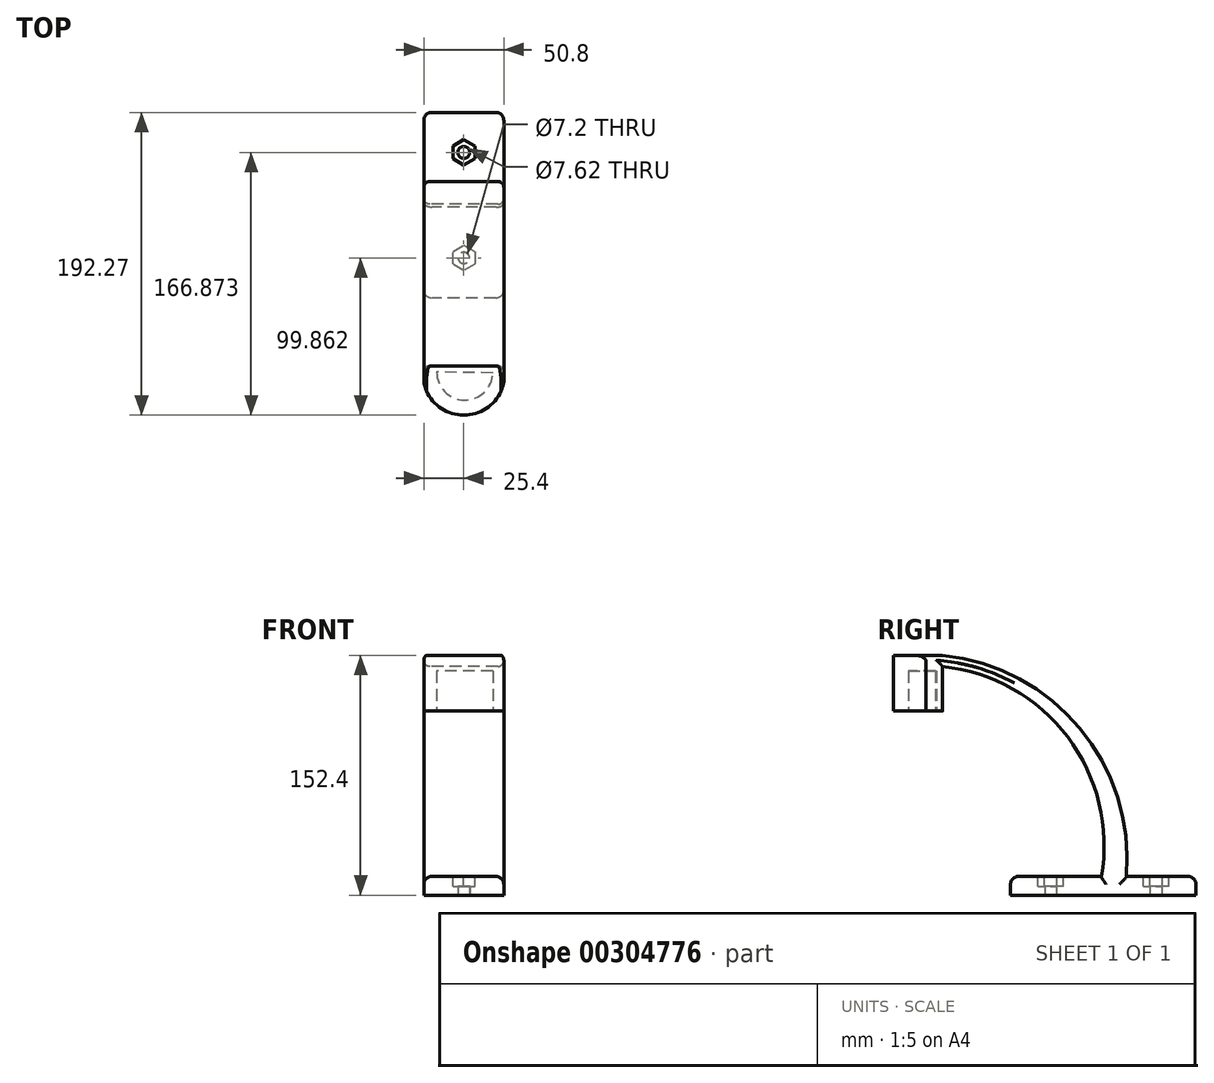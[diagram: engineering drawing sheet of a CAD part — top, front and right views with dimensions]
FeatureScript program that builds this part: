
annotation { "Feature Type Name" : "Feature", "Feature Type Description" : "" }
export const myFeature = defineFeature(function(context is Context, id is Id, definition is map)
    precondition{}
    {
        {
            var Q0;
            Q0=qCreatedBy(makeId("Right.planeOp"),FACE);
            var sketch = newSketch(context, id + "F0", { "sketchPlane" : qUnion([Q0])});
            skLineSegment(sketch, "E0.bottom", {"start": v(-57.77, 0) * mm, "end": v(60.04, 0) * mm});
            skLineSegment(sketch, "E0.top", {"start": v(-57.77, 11.91) * mm, "end": v(60.04, 11.91) * mm});
            skLineSegment(sketch, "E0.left", {"start": v(-57.77, 0) * mm, "end": v(-57.77, 11.91) * mm});
            skLineSegment(sketch, "E0.right", {"start": v(60.04, 0) * mm, "end": v(60.04, 11.91) * mm});
            skLineSegment(sketch, "E1.bottom", {"start": v(-132.44, 117) * mm, "end": v(-100.9, 117) * mm});
            skLineSegment(sketch, "E1.top", {"start": v(-132.44, 152.4) * mm, "end": v(-100.9, 152.4) * mm});
            skLineSegment(sketch, "E1.left", {"start": v(-132.44, 117) * mm, "end": v(-132.44, 152.4) * mm});
            skLineSegment(sketch, "E1.right", {"start": v(-100.9, 117) * mm, "end": v(-100.9, 152.4) * mm});
            skArc(sketch, "E2", {"start": v(15.8, 11.91) * mm, "mid": v(-13.86, 106) * mm, "end": v(-100.9, 152.4) * mm});
            skArc(sketch, "E3", {"start": v(0, 11.91) * mm, "mid": v(-21.52, 100.47) * mm, "end": v(-100.9, 145.2) * mm});
            skSolve(sketch);
        }
        {
            var Q0;
            Q0=qSketchRegion(id+"F0",true);
            extrude(context, id + "F1", {"entities" : qUnion([Q0]), "depth" : 50.8 * mm});
        }
        {
            var Q0;
            Q0=makeQuery(id+"F1.opExtrude","SWEPT_FACE",FACE,{"disambiguationData":[OSD([sQuery(id+"F0.wireOp",EDGE,"E1.top")])]});
            var sketch = newSketch(context, id + "F2", { "sketchPlane" : qUnion([Q0])});
            skArc(sketch, "E4", {"start": v(0, -100.9) * mm, "mid": v(25.4, -132.23) * mm, "end": v(50.8, -100.9) * mm});
            skSolve(sketch);
        }
        {
            var Q0;
            {var subQ0=sQuery(id+"F0.wireOp",EDGE,"E1.top");var subQ4=makeQuery(id+"F1.opExtrude","SWEPT_EDGE",EDGE,{"disambiguationData":[OSD([subQ0,sQuery(id+"F0.wireOp",EDGE,"E1.left")])]});Q0=makeQuery(id+"F2.imprint","IMPRINT",FACE,{"disambiguationData":[TD([[makeQuery(id+"F2.imprint","IMPRINT",EDGE,{"derivedFrom":subQ4}),-1.0]])]});}
            extrude(context, id + "F3", {"entities" : qUnion([Q0]), "operationType" : NewBodyOperationType.REMOVE, "endBound" : BoundingType.UP_TO_NEXT, "oppositeDirection" : true, "depth" : 25.4 * mm});
        }
        {
            var Q0;
            Q0=makeQuery(id+"F1.opExtrude","CAP_EDGE",EDGE,{"disambiguationData":[OSD([sQuery(id+"F0.wireOp",EDGE,"E1.right")])],"isStart":false});
            var Q1;
            Q1=makeQuery(id+"F1.opExtrude","CAP_EDGE",EDGE,{"disambiguationData":[OSD([sQuery(id+"F0.wireOp",EDGE,"E1.right")])],"isStart":true});
            var Q2;
            Q2=makeQuery(id+"F1.opExtrude","CAP_EDGE",EDGE,{"disambiguationData":[OSD([sQuery(id+"F0.wireOp",EDGE,"E3")])],"isStart":false});
            var Q3;
            Q3=makeQuery(id+"F1.opExtrude","CAP_EDGE",EDGE,{"disambiguationData":[OSD([sQuery(id+"F0.wireOp",EDGE,"E2")])],"isStart":false});
            var Q4;
            Q4=makeQuery(id+"F3.boolean.opBoolean","COPY",EDGE,{"derivedFrom":makeQuery(id+"F3.opExtrude","CAP_EDGE",EDGE,{"disambiguationData":[OSD([sQuery(id+"F2.wireOp",EDGE,"E4")])],"isStart":false})});
            var Q5;
            Q5=makeQuery(id+"F1.opExtrude","CAP_EDGE",EDGE,{"disambiguationData":[OSD([sQuery(id+"F0.wireOp",EDGE,"E3")])],"isStart":true});
            var Q6;
            Q6=makeQuery(id+"F1.opExtrude","CAP_EDGE",EDGE,{"disambiguationData":[OSD([sQuery(id+"F0.wireOp",EDGE,"E2")])],"isStart":true});
            fillet(context, id + "F4", {"entities" : qUnion([Q0, Q1, Q2, Q3, Q4, Q5, Q6]), "radius" : 3.8 * mm, "tangentPropagation" : true, "allowEdgeOverflow" : false});
        }
        {
            var Q0;
            Q0=makeQuery(id+"F1.opExtrude","SWEPT_FACE",FACE,{"disambiguationData":[OSD([sQuery(id+"F0.wireOp",EDGE,"E1.bottom")])]});
            var sketch = newSketch(context, id + "F5", { "sketchPlane" : qUnion([Q0])});
            skArc(sketch, "E5", {"start": v(43.42, 100.9) * mm, "mid": v(26.02, 122.66) * mm, "end": v(8.61, 100.9) * mm});
            skLineSegment(sketch, "E6", {"start": v(43.84, 105.46) * mm, "end": v(8.18, 104.82) * mm});
            skSolve(sketch);
        }
        {
            var Q0;
            {var subQ0=sQuery(id+"F5.wireOp",EDGE,"E6");Q0=makeQuery(id+"F5.imprint","IMPRINT",FACE,{"disambiguationData":[TD([[makeQuery(id+"F5.imprint","IMPRINT",EDGE,{"derivedFrom":subQ0}),-1.0]])]});}
            extrude(context, id + "F6", {"entities" : qUnion([Q0]), "operationType" : NewBodyOperationType.REMOVE, "oppositeDirection" : true, "depth" : 25.4 * mm});
        }
        {
            var Q0;
            {var subQ0=sQuery(id+"F0.wireOp",EDGE,"E0.top");Q0=makeQuery(id+"F1.opExtrude","SWEPT_FACE",FACE,{"disambiguationData":[OSD([subQ0]),TDD([makeQuery(id+"F0.imprint","IMPRINT",EDGE,{"disambiguationData":[TD([[makeQuery(id+"F0.imprint","INTERSECT",VERTEX,{"derivedFrom":[subQ0,sQuery(id+"F0.wireOp",EDGE,"E0.left")]}),-1.0]])],"derivedFrom":subQ0})])]});}
            var sketch = newSketch(context, id + "F7", { "sketchPlane" : qUnion([Q0])});
            skCircle(sketch, "E7.cCircle", {"center": v(25.4, -32.37) * mm, "radius": 6.99 * mm, "construction": true});
            skLineSegment(sketch, "E7.0", {"start": v(32.39, -28.33) * mm, "end": v(32.39, -36.4) * mm});
            skLineSegment(sketch, "E7.1", {"start": v(32.39, -36.4) * mm, "end": v(25.4, -40.43) * mm});
            skLineSegment(sketch, "E7.2", {"start": v(25.4, -40.43) * mm, "end": v(18.41, -36.4) * mm});
            skLineSegment(sketch, "E7.3", {"start": v(18.41, -36.4) * mm, "end": v(18.41, -28.33) * mm});
            skLineSegment(sketch, "E7.4", {"start": v(18.41, -28.33) * mm, "end": v(25.4, -24.3) * mm});
            skLineSegment(sketch, "E7.5", {"start": v(25.4, -24.3) * mm, "end": v(32.39, -28.33) * mm});
            skPoint(sketch, "E7.0.midPoint", {"position": v(32.39, -32.37) * mm});
            skSolve(sketch);
        }
        {
            var Q0;
            {var subQ0=sQuery(id+"F0.wireOp",EDGE,"E0.top");Q0=makeQuery(id+"F1.opExtrude","SWEPT_FACE",FACE,{"disambiguationData":[OSD([subQ0]),TDD([makeQuery(id+"F0.imprint","IMPRINT",EDGE,{"disambiguationData":[TD([[makeQuery(id+"F0.imprint","INTERSECT",VERTEX,{"derivedFrom":[subQ0,sQuery(id+"F0.wireOp",EDGE,"E0.right")]}),1.0]])],"derivedFrom":subQ0})])]});}
            var sketch = newSketch(context, id + "F8", { "sketchPlane" : qUnion([Q0])});
            skCircle(sketch, "E8.cCircle", {"center": v(25.4, 34.64) * mm, "radius": 6.98 * mm, "construction": true});
            skLineSegment(sketch, "E8.0", {"start": v(32.38, 38.68) * mm, "end": v(32.38, 30.6) * mm});
            skLineSegment(sketch, "E8.1", {"start": v(32.39, 30.6) * mm, "end": v(25.4, 26.58) * mm});
            skLineSegment(sketch, "E8.2", {"start": v(25.4, 26.58) * mm, "end": v(18.41, 30.6) * mm});
            skLineSegment(sketch, "E8.3", {"start": v(18.41, 30.6) * mm, "end": v(18.41, 38.68) * mm});
            skLineSegment(sketch, "E8.4", {"start": v(18.41, 38.68) * mm, "end": v(25.4, 42.7) * mm});
            skLineSegment(sketch, "E8.5", {"start": v(25.4, 42.7) * mm, "end": v(32.38, 38.68) * mm});
            skPoint(sketch, "E8.0.midPoint", {"position": v(32.38, 34.64) * mm});
            skSolve(sketch);
        }
        {
            var Q0;
            Q0=makeQuery(id+"F7.imprint","IMPRINT",FACE,{"disambiguationData":[TD([[makeQuery(id+"F7.imprint","IMPRINT",EDGE,{"derivedFrom":sQuery(id+"F7.wireOp",EDGE,"E7.0")}),-1.0]])]});
            var Q1;
            Q1=makeQuery(id+"F8.imprint","IMPRINT",FACE,{"disambiguationData":[TD([[makeQuery(id+"F8.imprint","IMPRINT",EDGE,{"derivedFrom":sQuery(id+"F8.wireOp",EDGE,"E8.0")}),-1.0]])]});
            extrude(context, id + "F9", {"entities" : qUnion([Q0, Q1]), "operationType" : NewBodyOperationType.REMOVE, "oppositeDirection" : true, "depth" : 6.35 * mm});
        }
        {
            var Q0;
            Q0=makeQuery(id+"F1.opExtrude","CAP_EDGE",EDGE,{"disambiguationData":[OSD([sQuery(id+"F0.wireOp",EDGE,"E0.right")])],"isStart":false});
            var Q1;
            Q1=makeQuery(id+"F1.opExtrude","CAP_EDGE",EDGE,{"disambiguationData":[OSD([sQuery(id+"F0.wireOp",EDGE,"E0.left")])],"isStart":false});
            var Q2;
            Q2=makeQuery(id+"F1.opExtrude","CAP_EDGE",EDGE,{"disambiguationData":[OSD([sQuery(id+"F0.wireOp",EDGE,"E0.right")])],"isStart":true});
            var Q3;
            Q3=makeQuery(id+"F1.opExtrude","CAP_EDGE",EDGE,{"disambiguationData":[OSD([sQuery(id+"F0.wireOp",EDGE,"E0.left")])],"isStart":true});
            var Q4;
            {var subQ0=sQuery(id+"F0.wireOp",EDGE,"E0.top");Q4=makeQuery(id+"F1.opExtrude","CAP_EDGE",EDGE,{"disambiguationData":[OSD([subQ0]),TDD([makeQuery(id+"F0.imprint","IMPRINT",EDGE,{"disambiguationData":[TD([[makeQuery(id+"F0.imprint","INTERSECT",VERTEX,{"derivedFrom":[subQ0,sQuery(id+"F0.wireOp",EDGE,"E0.right")]}),1.0]])],"derivedFrom":subQ0})])],"isStart":true});}
            var Q5;
            {var subQ0=sQuery(id+"F0.wireOp",EDGE,"E0.top");Q5=makeQuery(id+"F1.opExtrude","CAP_EDGE",EDGE,{"disambiguationData":[OSD([subQ0]),TDD([makeQuery(id+"F0.imprint","IMPRINT",EDGE,{"disambiguationData":[TD([[makeQuery(id+"F0.imprint","INTERSECT",VERTEX,{"derivedFrom":[subQ0,sQuery(id+"F0.wireOp",EDGE,"E0.left")]}),-1.0]])],"derivedFrom":subQ0})])],"isStart":true});}
            var Q6;
            {var subQ0=sQuery(id+"F0.wireOp",EDGE,"E0.top");Q6=makeQuery(id+"F1.opExtrude","CAP_EDGE",EDGE,{"disambiguationData":[OSD([subQ0]),TDD([makeQuery(id+"F0.imprint","IMPRINT",EDGE,{"disambiguationData":[TD([[makeQuery(id+"F0.imprint","INTERSECT",VERTEX,{"derivedFrom":[subQ0,sQuery(id+"F0.wireOp",EDGE,"E0.right")]}),1.0]])],"derivedFrom":subQ0})])],"isStart":false});}
            var Q7;
            {var subQ0=sQuery(id+"F0.wireOp",EDGE,"E0.top");Q7=makeQuery(id+"F1.opExtrude","CAP_EDGE",EDGE,{"disambiguationData":[OSD([subQ0]),TDD([makeQuery(id+"F0.imprint","IMPRINT",EDGE,{"disambiguationData":[TD([[makeQuery(id+"F0.imprint","INTERSECT",VERTEX,{"derivedFrom":[subQ0,sQuery(id+"F0.wireOp",EDGE,"E0.left")]}),-1.0]])],"derivedFrom":subQ0})])],"isStart":false});}
            var Q8;
            Q8=makeQuery(id+"F1.opExtrude","SWEPT_EDGE",EDGE,{"disambiguationData":[OSD([sQuery(id+"F0.wireOp",EDGE,"E0.top"),sQuery(id+"F0.wireOp",EDGE,"E0.left")])]});
            var Q9;
            Q9=makeQuery(id+"F1.opExtrude","SWEPT_EDGE",EDGE,{"disambiguationData":[OSD([sQuery(id+"F0.wireOp",EDGE,"E0.top"),sQuery(id+"F0.wireOp",EDGE,"E0.right")])]});
            fillet(context, id + "F10", {"entities" : qUnion([Q0, Q1, Q2, Q3, Q4, Q5, Q6, Q7, Q8, Q9]), "radius" : 5.08 * mm, "tangentPropagation" : true, "allowEdgeOverflow" : false});
        }
        {
            var Q0;
            Q0=makeQuery(id+"F1.opExtrude","SWEPT_FACE",FACE,{"disambiguationData":[OSD([sQuery(id+"F0.wireOp",EDGE,"E0.bottom")])]});
            var sketch = newSketch(context, id + "F11", { "sketchPlane" : qUnion([Q0])});
            skCircle(sketch, "E9", {"center": v(25.4, 32.37) * mm, "radius": 3.6 * mm});
            skCircle(sketch, "E10", {"center": v(25.4, -34.64) * mm, "radius": 3.81 * mm});
            skSolve(sketch);
        }
        {
            var Q0;
            Q0=makeQuery(id+"F11.imprint","IMPRINT",FACE,{"disambiguationData":[TD([[makeQuery(id+"F11.imprint","IMPRINT",EDGE,{"derivedFrom":sQuery(id+"F11.wireOp",EDGE,"E10")}),1.0]])]});
            var Q1;
            Q1=makeQuery(id+"F11.imprint","IMPRINT",FACE,{"disambiguationData":[TD([[makeQuery(id+"F11.imprint","IMPRINT",EDGE,{"derivedFrom":sQuery(id+"F11.wireOp",EDGE,"E9")}),1.0]])]});
            extrude(context, id + "F12", {"entities" : qUnion([Q0, Q1]), "operationType" : NewBodyOperationType.REMOVE, "endBound" : BoundingType.UP_TO_NEXT, "oppositeDirection" : true, "depth" : 25.4 * mm});
        }
    });
